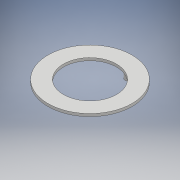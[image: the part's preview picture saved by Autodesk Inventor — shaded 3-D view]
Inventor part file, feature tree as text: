
AUTODESK INVENTOR PART (.ipt)
format: ipt  version: 2018 (Build 220112000, 112)  size: 135,168 bytes
history: native  units: mm
features: sketch x3, extrude x3
ambient origin geometry x8: Origin, YZ Plane, XZ Plane, XY Plane, X Axis, Y Axis, Z Axis, Center Point
bodies: Solide1 (feature_tree)
feature tree (6):
  sketch  "Esquisse1"
  sketch  "Esquisse2"
  extrude  "Extrusion1"  Depth=95.0mm
  extrude  "Extrusion2"  Depth=60.0mm
  extrude  "Extrusion3"  Depth=2.5mm
  sketch  "Esquisse3"
